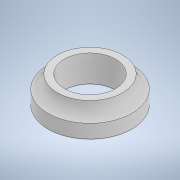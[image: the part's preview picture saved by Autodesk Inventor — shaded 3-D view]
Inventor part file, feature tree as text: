
AUTODESK INVENTOR PART (.ipt)
format: ipt  version: 2021 (Build 250183000, 183)  size: 143,872 bytes
history: native  units: in
note: dims shown in document units (in); Inventor stores cm internally (conversion verified against a paired STEP export)
features: revolve x1, fillet x1, sketch x1
ambient origin geometry x8: Origin, YZ Plane, XZ Plane, XY Plane, X Axis, Y Axis, Z Axis, Center Point
bodies: Solid1 (feature_tree)
feature tree (3):
  revolve  "Revolution1"  [1 undecoded]
  fillet  "Fillet1"  Radius=0.4331in
  sketch  "Sketch1"  dims[d0=0.7087in d1=0.4724in d2=0.4331in d3=0.0787in d4=0.2362in d5=90.0deg d6=0.0197in]
note: 1 required parameter value undecoded (feature->parameter linkage not recoverable at this tier; creation-order binding heuristic only, values carry confidence <= 0.55)
